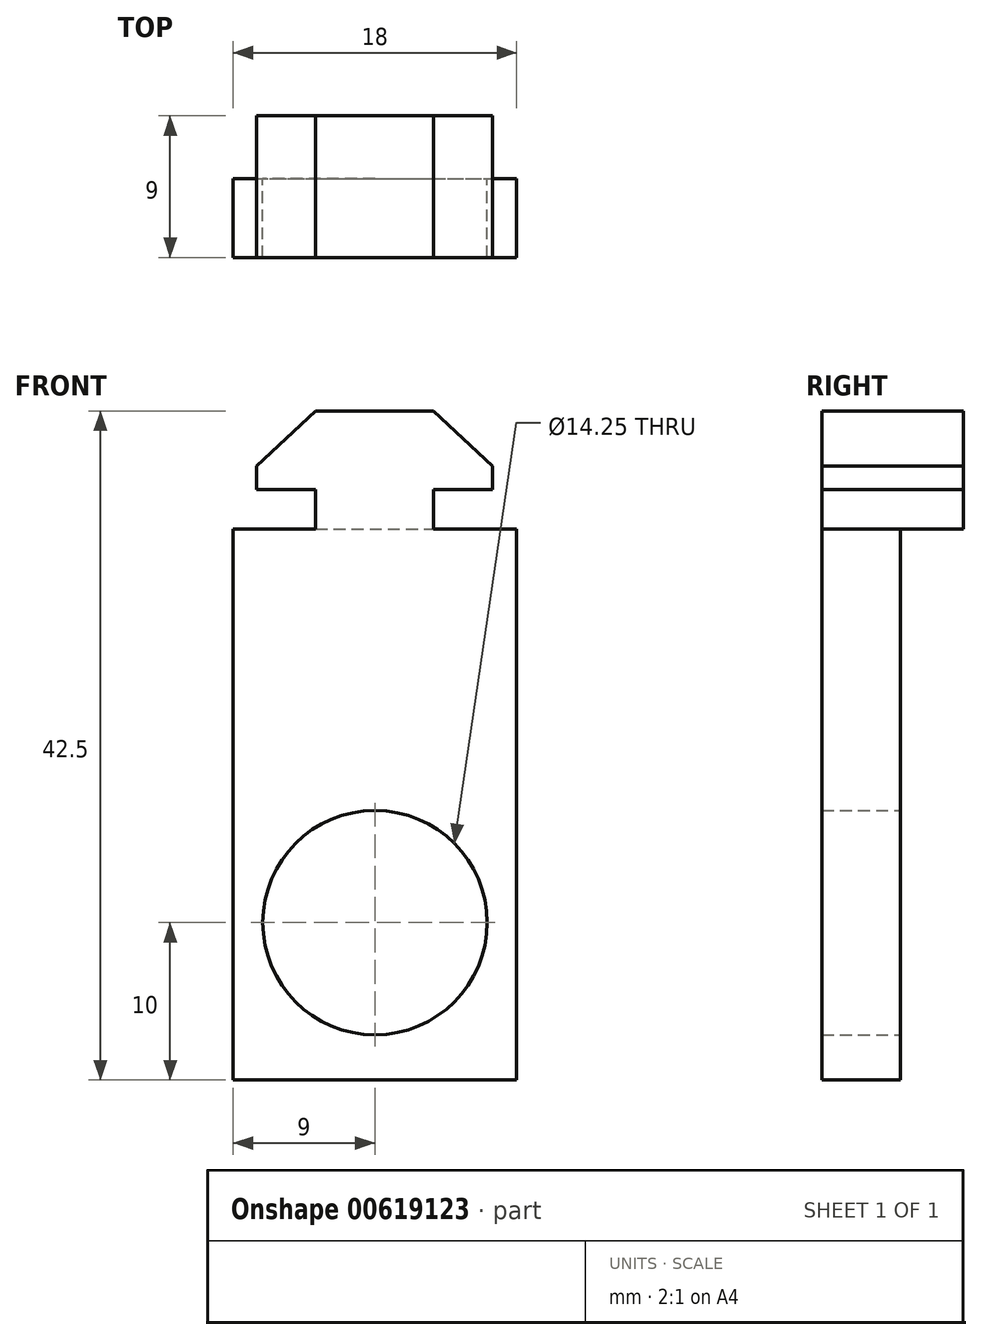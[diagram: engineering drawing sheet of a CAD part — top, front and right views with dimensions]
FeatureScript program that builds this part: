
annotation { "Feature Type Name" : "Feature", "Feature Type Description" : "" }
export const myFeature = defineFeature(function(context is Context, id is Id, definition is map)
    precondition{}
    {
        {
            var Q0;
            Q0=qCreatedBy(makeId("Front.planeOp"),FACE);
            var sketch = newSketch(context, id + "F0", { "sketchPlane" : qUnion([Q0])});
            skLineSegment(sketch, "E0", {"start": v(-3.77, 0) * mm, "end": v(-3.77, 2.5) * mm});
            skLineSegment(sketch, "E1", {"start": v(-3.77, 2.5) * mm, "end": v(-7.52, 2.5) * mm});
            skLineSegment(sketch, "E2", {"start": v(-7.52, 2.5) * mm, "end": v(-7.52, 4) * mm});
            skLineSegment(sketch, "E3", {"start": v(-7.52, 4) * mm, "end": v(-3.77, 7.5) * mm});
            skLineSegment(sketch, "E4", {"start": v(-3.77, 7.5) * mm, "end": v(3.73, 7.5) * mm});
            skLineSegment(sketch, "E5", {"start": v(3.73, 7.5) * mm, "end": v(7.48, 4) * mm});
            skLineSegment(sketch, "E6", {"start": v(7.48, 4) * mm, "end": v(7.48, 2.5) * mm});
            skLineSegment(sketch, "E7", {"start": v(7.48, 2.5) * mm, "end": v(3.73, 2.5) * mm});
            skLineSegment(sketch, "E8", {"start": v(3.73, 2.5) * mm, "end": v(3.73, 0) * mm});
            skLineSegment(sketch, "E9", {"start": v(3.73, 0) * mm, "end": v(-3.77, 0) * mm});
            skSolve(sketch);
        }
        {
            var Q0;
            Q0=qSketchRegion(id+"F0",true);
            extrude(context, id + "F1", {"entities" : qUnion([Q0]), "depth" : 9 * mm, "offsetDistance" : 25 * mm});
        }
        {
            var Q0;
            Q0=makeQuery(id+"F1.opExtrude","CAP_FACE",FACE,{"disambiguationData":[OSD([sQuery(id+"F0.wireOp",EDGE,"E0"),sQuery(id+"F0.wireOp",EDGE,"E1"),sQuery(id+"F0.wireOp",EDGE,"E2"),sQuery(id+"F0.wireOp",EDGE,"E3"),sQuery(id+"F0.wireOp",EDGE,"E4"),sQuery(id+"F0.wireOp",EDGE,"E5"),sQuery(id+"F0.wireOp",EDGE,"E6"),sQuery(id+"F0.wireOp",EDGE,"E7"),sQuery(id+"F0.wireOp",EDGE,"E8"),sQuery(id+"F0.wireOp",EDGE,"E9")])],"isStart":false});
            var sketch = newSketch(context, id + "F2", { "sketchPlane" : qUnion([Q0])});
            skLineSegment(sketch, "E10.bottom", {"start": v(-9, 0) * mm, "end": v(9, 0) * mm});
            skLineSegment(sketch, "E10.top", {"start": v(-9, -35) * mm, "end": v(9, -35) * mm});
            skLineSegment(sketch, "E10.left", {"start": v(-9, 0) * mm, "end": v(-9, -35) * mm});
            skLineSegment(sketch, "E10.right", {"start": v(9, 0) * mm, "end": v(9, -35) * mm});
            skSolve(sketch);
        }
        {
            var Q0;
            Q0=qSketchRegion(id+"F2",true);
            extrude(context, id + "F3", {"entities" : qUnion([Q0]), "operationType" : NewBodyOperationType.ADD, "oppositeDirection" : true, "depth" : 5 * mm, "offsetDistance" : 25 * mm});
        }
        {
            var Q0;
            Q0=makeQuery(id+"F3.boolean.opBoolean","MERGE",FACE,{"derivedFrom":[makeQuery(id+"F1.opExtrude","CAP_FACE",FACE,{"disambiguationData":[OSD([sQuery(id+"F0.wireOp",EDGE,"E0"),sQuery(id+"F0.wireOp",EDGE,"E1"),sQuery(id+"F0.wireOp",EDGE,"E2"),sQuery(id+"F0.wireOp",EDGE,"E3"),sQuery(id+"F0.wireOp",EDGE,"E4"),sQuery(id+"F0.wireOp",EDGE,"E5"),sQuery(id+"F0.wireOp",EDGE,"E6"),sQuery(id+"F0.wireOp",EDGE,"E7"),sQuery(id+"F0.wireOp",EDGE,"E8"),sQuery(id+"F0.wireOp",EDGE,"E9")])],"isStart":false}),makeQuery(id+"F3.opExtrude","CAP_FACE",FACE,{"disambiguationData":[OSD([sQuery(id+"F2.wireOp",EDGE,"E10.bottom"),sQuery(id+"F2.wireOp",EDGE,"E10.top"),sQuery(id+"F2.wireOp",EDGE,"E10.left"),sQuery(id+"F2.wireOp",EDGE,"E10.right")])],"isStart":true})]});
            var sketch = newSketch(context, id + "F4", { "sketchPlane" : qUnion([Q0])});
            skPoint(sketch, "E11", {"position": v(0, -25) * mm});
            skSolve(sketch);
        }
        {
            var Q0;
            Q0=sQuery(id+"F4.wireOp",VERTEX,"E11");
            var Q1;
            Q1=makeQuery(id+"F1.opExtrude","SWEPT_BODY",BODY,{"disambiguationData":[OSD([sQuery(id+"F0.wireOp",EDGE,"E0"),sQuery(id+"F0.wireOp",EDGE,"E1"),sQuery(id+"F0.wireOp",EDGE,"E2"),sQuery(id+"F0.wireOp",EDGE,"E3"),sQuery(id+"F0.wireOp",EDGE,"E4"),sQuery(id+"F0.wireOp",EDGE,"E5"),sQuery(id+"F0.wireOp",EDGE,"E6"),sQuery(id+"F0.wireOp",EDGE,"E7"),sQuery(id+"F0.wireOp",EDGE,"E8"),sQuery(id+"F0.wireOp",EDGE,"E9")])]});
            hole(context, id + "F5", {"style" : HoleStyle.C_BORE, "endStyle" : HoleEndStyle.BLIND, "standardTappedOrClearance" : lookupTablePath({ "standard" : "ISO", "fit" : "Normal", "size" : "M8", "type" : "Clearance" }), "standardBlindInLast" : lookupTablePath({ "fit" : "Standard", "standard" : "ISO", "size" : "M8", "type" : "Clearance" }), "holeDiameter" : 8.8 * mm, "cBoreDiameter" : 14.25 * mm, "cBoreDepth" : 8 * mm, "majorDiameter" : 5 * mm, "holeDepth" : 10 * mm, "isTappedThrough" : true, "tappedDepth" : 12 * mm, "tapClearance" : 3, "locations" : qUnion([Q0]), "scope" : qUnion([Q1]), "startStyle" : HoleStartStyle.SKETCH});
        }
    });
